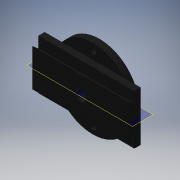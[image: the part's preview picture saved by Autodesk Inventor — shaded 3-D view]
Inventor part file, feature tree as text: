
AUTODESK INVENTOR PART (.ipt)
format: ipt  version: 2018 (Build 220112000, 112)  size: 176,128 bytes
history: native  units: mm
features: extrude x6, sketch x6, plane x1
ambient origin geometry x8: Origin, YZ Plane, XZ Plane, XY Plane, X Axis, Y Axis, Z Axis, Center Point
bodies: Solid1 (feature_tree)
feature tree (13):
  extrude  "Extrusion1"  Depth=19.0mm
  extrude  "Extrusion2"  Depth=165.2mm
  extrude  "Extrusion3"  Depth=11.5mm TaperAngle=0.0deg
  extrude  "Extrusion4"  Depth=73.75mm TaperAngle=0.0deg
  extrude  "Extrusion5"  Depth=6.0mm
  extrude  "Extrusion6"  Depth=5.4mm
  plane  "Work Plane1"
  sketch  "Sketch1"  dims[d1=85.6mm d7=19.0mm]
  sketch  "Sketch3"  dims[d8=165.2mm d9=0.0mm d10=14.0mm]
  sketch  "Sketch4"  dims[d11=68.3mm d12=11.5mm d13=0.0mm]
  sketch  "Sketch5"  dims[d14=18.3mm d15=73.75mm d16=0.0mm]
  sketch  "Sketch7"  dims[d17=6.0mm d18=6.0mm]
  sketch  "Sketch8"  dims[d19=5.4mm d20=5.4mm d21=73.75mm d22=0.0mm d23=6.9mm d24=10.8mm d25=6.0mm d26=0.0mm d27=6.2mm d28=22.8mm d29=0.0mm d30=8.726646mm d31=19.0mm d32=8.726646mm d33=10.0mm]
